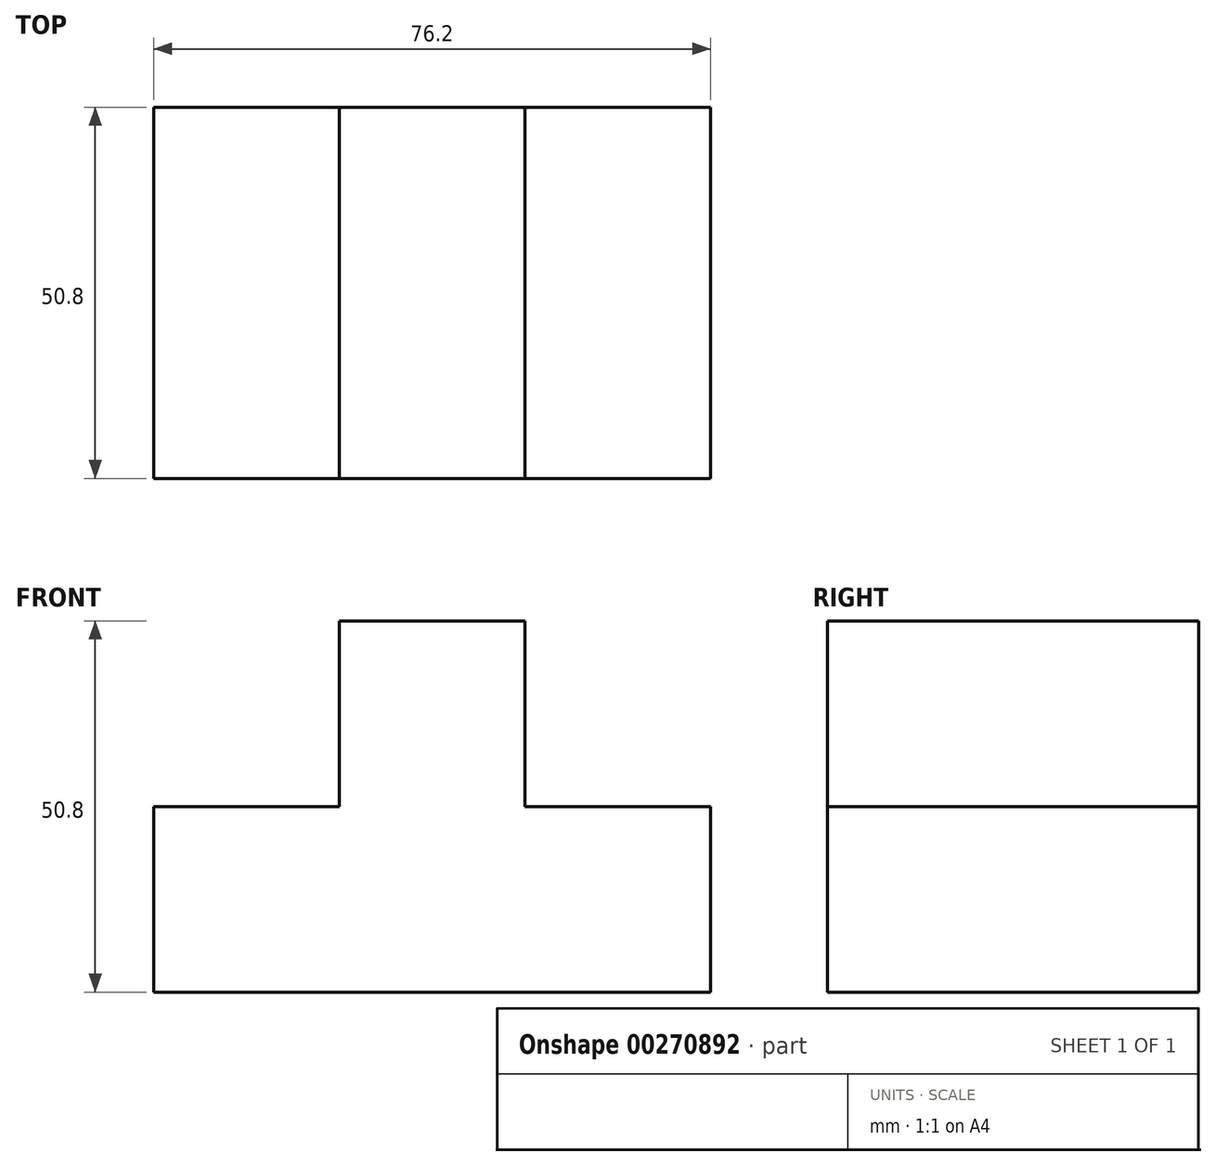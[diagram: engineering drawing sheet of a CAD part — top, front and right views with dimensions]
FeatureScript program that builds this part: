
annotation { "Feature Type Name" : "Feature", "Feature Type Description" : "" }
export const myFeature = defineFeature(function(context is Context, id is Id, definition is map)
    precondition{}
    {
        {
            var Q0;
            Q0=qCreatedBy(makeId("Front.planeOp"),FACE);
            var sketch = newSketch(context, id + "F0", { "sketchPlane" : qUnion([Q0])});
            skLineSegment(sketch, "E0", {"start": v(0, 0) * mm, "end": v(-76.2, 0) * mm});
            skLineSegment(sketch, "E1", {"start": v(-76.2, 0) * mm, "end": v(-76.2, 25.4) * mm});
            skLineSegment(sketch, "E2", {"start": v(-76.2, 25.4) * mm, "end": v(-50.8, 25.4) * mm});
            skLineSegment(sketch, "E3", {"start": v(-50.8, 25.4) * mm, "end": v(-50.8, 50.8) * mm});
            skLineSegment(sketch, "E4", {"start": v(-50.8, 50.8) * mm, "end": v(-25.4, 50.8) * mm});
            skLineSegment(sketch, "E5", {"start": v(0, 0) * mm, "end": v(0, 25.4) * mm});
            skLineSegment(sketch, "E6", {"start": v(0, 25.4) * mm, "end": v(-25.4, 25.4) * mm});
            skLineSegment(sketch, "E7", {"start": v(-25.4, 25.4) * mm, "end": v(-25.4, 50.8) * mm});
            skSolve(sketch);
        }
        {
            var Q0;
            Q0 = qSketchRegion(id + "F0", true);
            extrude(context, id + "F1", {"entities" : qUnion([Q0]), "depth" : 50.8 * mm});
        }
    });
